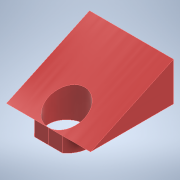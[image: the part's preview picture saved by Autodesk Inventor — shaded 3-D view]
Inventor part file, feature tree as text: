
AUTODESK INVENTOR PART (.ipt)
format: ipt  version: 2022.2 (Build 262287000, 287)  size: 153,600 bytes
history: native  units: mm
features: extrude x3, sketch x2
ambient origin geometry x8: Origin, YZ Plane, XZ Plane, XY Plane, X Axis, Y Axis, Z Axis, Center Point
bodies: Solid6 (feature_tree)
feature tree (5):
  extrude  "Extrusion34"  Depth=139.7mm TaperAngle=0.0deg
  sketch  "Sketch67"  dims[d338=60.325mm d339=8.0mm d344=8.0mm d345=0.0mm d346=0.0mm d347=25.0mm d348=0.0mm d349=152.4mm d64=1.0mm d65=1.0mm d66=1.0mm d67=0.15mm d68=0.25mm d69=0.375mm d70=14.3117mm d71=0.75mm d72=20.594885mm d73=0.0625mm d74=0.75mm d75=0.375mm]
  extrude  "Extrusion37"  Depth=152.4mm
  extrude  "Extrusion38"  Depth=152.4mm
  sketch  "Sketch65"  dims[d335=4.363323mm d336=139.7mm d337=0.0mm]
